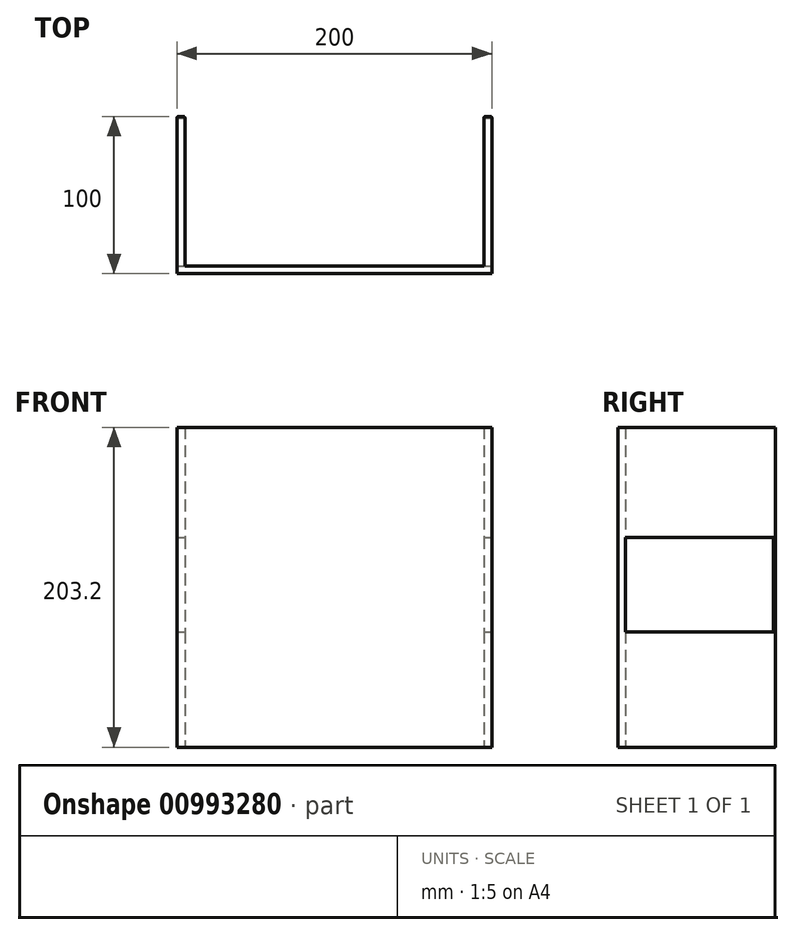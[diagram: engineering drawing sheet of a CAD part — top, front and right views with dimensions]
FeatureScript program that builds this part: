
annotation { "Feature Type Name" : "Feature", "Feature Type Description" : "" }
export const myFeature = defineFeature(function(context is Context, id is Id, definition is map)
    precondition{}
    {
        {
            var Q0;
            Q0=qCreatedBy(makeId("Top.planeOp"),FACE);
            var sketch = newSketch(context, id + "F0", { "sketchPlane" : qUnion([Q0])});
            skLineSegment(sketch, "E0", {"start": v(-258.03, 0) * mm, "end": v(-258.03, 95) * mm});
            skLineSegment(sketch, "E1", {"start": v(-258.03, 95) * mm, "end": v(-263.03, 95) * mm});
            skLineSegment(sketch, "E2", {"start": v(-263.03, 95) * mm, "end": v(-263.03, -5) * mm});
            skLineSegment(sketch, "E3", {"start": v(-263.03, -5) * mm, "end": v(-63.03, -5) * mm});
            skLineSegment(sketch, "E4", {"start": v(-63.03, -5) * mm, "end": v(-63.03, 95) * mm});
            skLineSegment(sketch, "E5", {"start": v(-63.03, 95) * mm, "end": v(-68.03, 95) * mm});
            skLineSegment(sketch, "E6", {"start": v(-68.03, 95) * mm, "end": v(-68.03, 0) * mm});
            skLineSegment(sketch, "E7", {"start": v(-68.03, 0) * mm, "end": v(-258.03, 0) * mm});
            skSolve(sketch);
        }
        {
            var Q0;
            Q0 = qSketchRegion(id + "F0", true);
            extrude(context, id + "F1", {"entities" : qUnion([Q0]), "depth" : 203.2 * mm, "offsetDistance" : 25.4 * mm});
        }
        {
            var Q0;
            Q0=makeQuery(id+"F1.opExtrude","SWEPT_EDGE",EDGE,{"disambiguationData":[OSD([sQuery(id+"F0.wireOp",EDGE,"E4"),sQuery(id+"F0.wireOp",EDGE,"E5")])]});
            var Q1;
            Q1=makeQuery(id+"F1.opExtrude","SWEPT_EDGE",EDGE,{"disambiguationData":[OSD([sQuery(id+"F0.wireOp",EDGE,"E5"),sQuery(id+"F0.wireOp",EDGE,"E6")])]});
            var Q2;
            Q2=makeQuery(id+"F1.opExtrude","SWEPT_EDGE",EDGE,{"disambiguationData":[OSD([sQuery(id+"F0.wireOp",EDGE,"E0"),sQuery(id+"F0.wireOp",EDGE,"E1")])]});
            var Q3;
            Q3=makeQuery(id+"F1.opExtrude","SWEPT_EDGE",EDGE,{"disambiguationData":[OSD([sQuery(id+"F0.wireOp",EDGE,"E1"),sQuery(id+"F0.wireOp",EDGE,"E2")])]});
            fillet(context, id + "F2", {"entities" : qUnion([Q0, Q1, Q2, Q3]), "radius" : 1 * mm, "tangentPropagation" : true, "allowEdgeOverflow" : false});
        }
        {
            var Q0;
            Q0=makeQuery(id+"F1.opExtrude","SWEPT_FACE",FACE,{"disambiguationData":[OSD([sQuery(id+"F0.wireOp",EDGE,"E4")])]});
            var sketch = newSketch(context, id + "F3", { "sketchPlane" : qUnion([Q0])});
            skLineSegment(sketch, "E8.bottom", {"start": v(94, 133.3) * mm, "end": v(0, 133.3) * mm});
            skLineSegment(sketch, "E8.top", {"start": v(94, 73.26) * mm, "end": v(0, 73.26) * mm});
            skLineSegment(sketch, "E8.left", {"start": v(94, 133.3) * mm, "end": v(94, 73.26) * mm});
            skLineSegment(sketch, "E8.right", {"start": v(0, 133.3) * mm, "end": v(0, 73.26) * mm});
            skSolve(sketch);
        }
        {
            var Q0;
            Q0=makeQuery(id+"F3.imprint","IMPRINT",FACE,{"disambiguationData":[TD([[makeQuery(id+"F3.imprint","IMPRINT",EDGE,{"derivedFrom":sQuery(id+"F3.wireOp",EDGE,"E8.bottom")}),1.0]])]});
            extrude(context, id + "F4", {"entities" : qUnion([Q0]), "operationType" : NewBodyOperationType.REMOVE, "oppositeDirection" : true, "depth" : 300 * mm, "offsetDistance" : 25.4 * mm});
        }
    });
